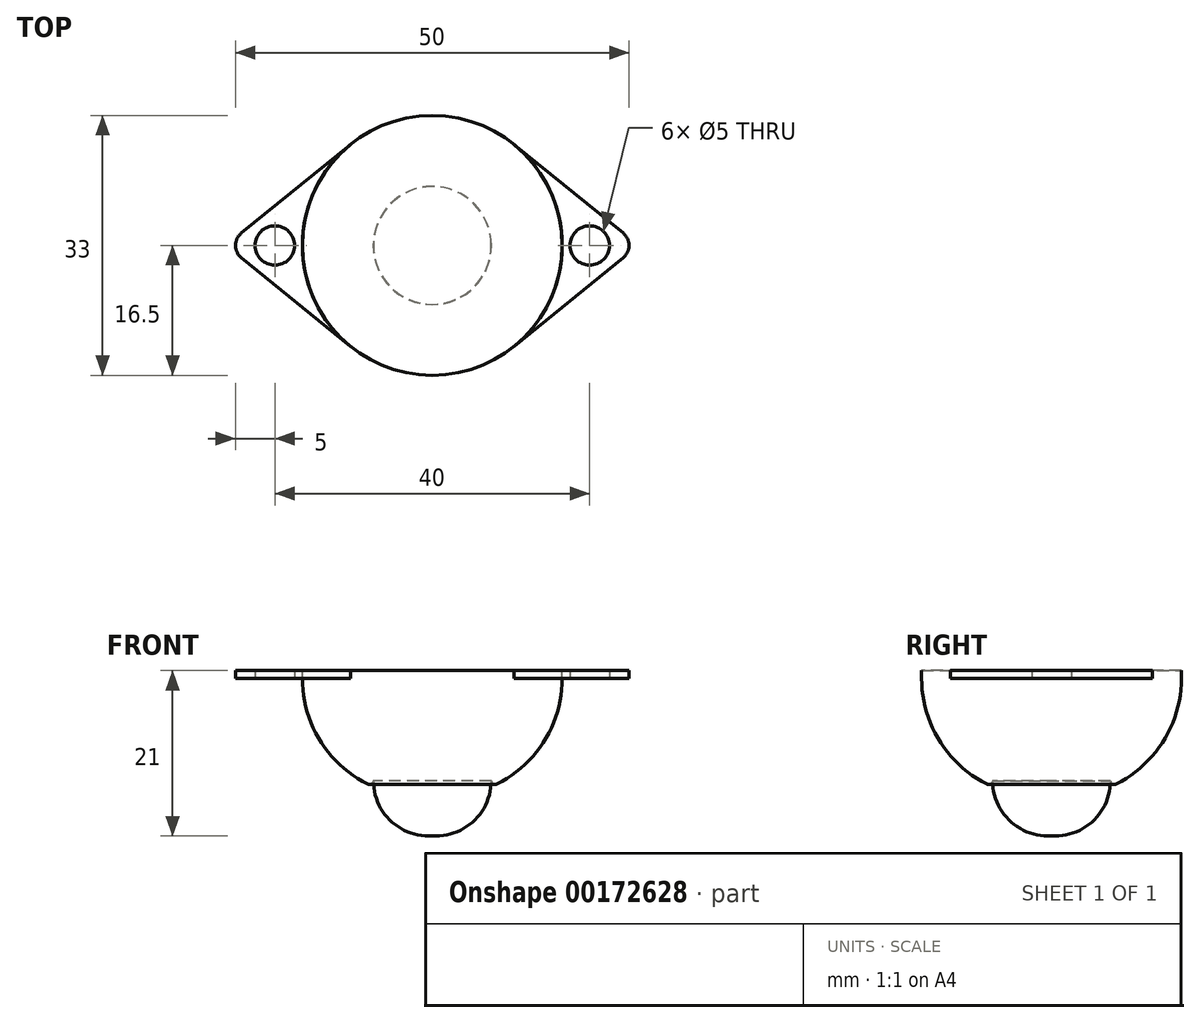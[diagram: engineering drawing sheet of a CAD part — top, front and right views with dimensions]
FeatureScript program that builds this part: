
annotation { "Feature Type Name" : "Feature", "Feature Type Description" : "" }
export const myFeature = defineFeature(function(context is Context, id is Id, definition is map)
    precondition{}
    {
        {
            var Q0;
            Q0=qCreatedBy(makeId("Top.planeOp"),FACE);
            var sketch = newSketch(context, id + "F0", { "sketchPlane" : qUnion([Q0])});
            skCircle(sketch, "E0", {"center": v(0, 0) * mm, "radius": 16.5 * mm});
            skPoint(sketch, "E1", {"position": v(-25, 0) * mm});
            skPoint(sketch, "E2.MirrorP", {"position": v(25, 0) * mm});
            skArc(sketch, "E3", {"start": v(-24.26, 1.55) * mm, "mid": v(-25, 0) * mm, "end": v(-24.26, -1.55) * mm});
            skArc(sketch, "E4", {"start": v(24.26, -1.55) * mm, "mid": v(25, 0) * mm, "end": v(24.26, 1.55) * mm});
            skLineSegment(sketch, "E5", {"start": v(-24.26, 1.55) * mm, "end": v(-10.4, 12.8) * mm});
            skLineSegment(sketch, "E6", {"start": v(-24.26, -1.55) * mm, "end": v(-10.4, -12.8) * mm});
            skLineSegment(sketch, "E7", {"start": v(10.4, 12.8) * mm, "end": v(24.26, 1.55) * mm});
            skPoint(sketch, "E8", {"position": v(-24.26, 1.55) * mm});
            skPoint(sketch, "E9", {"position": v(-24.26, -1.55) * mm});
            skPoint(sketch, "E10", {"position": v(24.26, 1.55) * mm});
            skLineSegment(sketch, "E11", {"start": v(24.26, -1.55) * mm, "end": v(10.4, -12.8) * mm});
            skPoint(sketch, "E12", {"position": v(24.26, -1.55) * mm});
            skSolve(sketch);
        }
        {
            var Q0;
            Q0=makeQuery(id+"F0.imprint","IMPRINT",FACE,{"disambiguationData":[TD([[makeQuery(id+"F0.imprint","IMPRINT",EDGE,{"derivedFrom":sQuery(id+"F0.wireOp",EDGE,"E3")}),1.0]])]});
            var Q1;
            Q1=makeQuery(id+"F0.imprint","IMPRINT",FACE,{"disambiguationData":[TD([[makeQuery(id+"F0.imprint","IMPRINT",EDGE,{"derivedFrom":sQuery(id+"F0.wireOp",EDGE,"E4")}),1.0]])]});
            extrude(context, id + "F1", {"entities" : qUnion([Q0, Q1]), "depth" : 1 * mm});
        }
        {
            var Q0;
            {var subQ0=sQuery(id+"F0.wireOp",EDGE,"E0");var subQ1=makeQuery(id+"F0.imprint","INTERSECT",VERTEX,{"derivedFrom":[subQ0,sQuery(id+"F0.wireOp",EDGE,"E5")]});Q0=makeQuery(id+"F0.imprint","IMPRINT",FACE,{"disambiguationData":[TD([[makeQuery(id+"F0.imprint","IMPRINT",EDGE,{"disambiguationData":[TD([[subQ1,1.0]])],"derivedFrom":subQ0}),1.0]])]});}
            extrude(context, id + "F2", {"entities" : qUnion([Q0]), "depth" : 16 * mm});
        }
        {
            var Q0;
            Q0=makeQuery(id+"F2.opExtrude","CAP_EDGE",EDGE,{"disambiguationData":[OSD([sQuery(id+"F0.wireOp",EDGE,"E0")])],"isStart":false});
            fillet(context, id + "F3", {"entities" : qUnion([Q0]), "radius" : 15 * mm, "tangentPropagation" : true, "allowEdgeOverflow" : false});
        }
        {
            var Q0;
            Q0=makeQuery(id+"F2.opExtrude","CAP_FACE",FACE,{"disambiguationData":[OSD([sQuery(id+"F0.wireOp",EDGE,"E0")])],"isStart":false});
            var sketch = newSketch(context, id + "F4", { "sketchPlane" : qUnion([Q0])});
            skCircle(sketch, "E13", {"center": v(0, 0) * mm, "radius": 7.5 * mm});
            skSolve(sketch);
        }
        {
            var Q0;
            Q0 = qSketchRegion(id + "F4", true);
            extrude(context, id + "F5", {"entities" : qUnion([Q0]), "operationType" : NewBodyOperationType.REMOVE, "oppositeDirection" : true, "depth" : 2 * mm});
        }
        {
            var Q0;
            Q0=makeQuery(id+"F5.boolean.opBoolean","INTERSECT",EDGE,{"derivedFrom":[makeQuery(id+"F3.opFillet","BLEND_FACE",FACE,{"disambiguationData":[OSD([sQuery(id+"F0.wireOp",EDGE,"E0")])]}),makeQuery(id+"F5.opExtrude","SWEPT_FACE",FACE,{"disambiguationData":[OSD([sQuery(id+"F4.wireOp",EDGE,"E13")])]})]});
            fillet(context, id + "F6", {"entities" : qUnion([Q0]), "radius" : 0.5 * mm, "tangentPropagation" : true, "allowEdgeOverflow" : false});
        }
        {
            var Q0;
            Q0=makeQuery(id+"F5.boolean.opBoolean","COPY",FACE,{"derivedFrom":makeQuery(id+"F5.opExtrude","CAP_FACE",FACE,{"disambiguationData":[OSD([sQuery(id+"F4.wireOp",EDGE,"E13")])],"isStart":false})});
            var sketch = newSketch(context, id + "F7", { "sketchPlane" : qUnion([Q0])});
            skCircle(sketch, "E14", {"center": v(0, 0) * mm, "radius": 7.48 * mm});
            skSolve(sketch);
        }
        {
            var Q0;
            Q0 = qSketchRegion(id + "F7", true);
            extrude(context, id + "F8", {"entities" : qUnion([Q0]), "operationType" : NewBodyOperationType.ADD, "depth" : 7 * mm});
        }
        {
            var Q0;
            Q0=makeQuery(id+"F8.opExtrude","CAP_FACE",FACE,{"disambiguationData":[OSD([sQuery(id+"F7.wireOp",EDGE,"E14")])],"isStart":false});
            fillet(context, id + "F9", {"entities" : qUnion([Q0]), "radius" : 7 * mm, "tangentPropagation" : true, "allowEdgeOverflow" : false});
        }
        {
            var Q0;
            Q0=makeQuery(id+"F1.opExtrude","CAP_FACE",FACE,{"disambiguationData":[OSD([sQuery(id+"F0.wireOp",EDGE,"E0"),sQuery(id+"F0.wireOp",EDGE,"E3"),sQuery(id+"F0.wireOp",EDGE,"E5"),sQuery(id+"F0.wireOp",EDGE,"E6")])],"isStart":false});
            var sketch = newSketch(context, id + "F10", { "sketchPlane" : qUnion([Q0])});
            skPoint(sketch, "E15", {"position": v(-20, 0) * mm});
            skCircle(sketch, "E16", {"center": v(-20, 0) * mm, "radius": 2.5 * mm});
            skSolve(sketch);
        }
        {
            var Q0;
            Q0=makeQuery(id+"F10.imprint","IMPRINT",FACE,{"disambiguationData":[TD([[makeQuery(id+"F10.imprint","IMPRINT",EDGE,{"derivedFrom":sQuery(id+"F10.wireOp",EDGE,"E16")}),1.0]])]});
            extrude(context, id + "F11", {"entities" : qUnion([Q0]), "operationType" : NewBodyOperationType.REMOVE, "oppositeDirection" : true, "depth" : 25.4 * mm});
        }
        {
            var Q0;
            Q0=makeQuery(id+"F1.opExtrude","CAP_FACE",FACE,{"disambiguationData":[OSD([sQuery(id+"F0.wireOp",EDGE,"E0"),sQuery(id+"F0.wireOp",EDGE,"E4"),sQuery(id+"F0.wireOp",EDGE,"E7"),sQuery(id+"F0.wireOp",EDGE,"E11")])],"isStart":false});
            var sketch = newSketch(context, id + "F12", { "sketchPlane" : qUnion([Q0])});
            skCircle(sketch, "E17", {"center": v(20, 0) * mm, "radius": 2.5 * mm});
            skSolve(sketch);
        }
        {
            var Q0;
            Q0 = qSketchRegion(id + "F12", true);
            extrude(context, id + "F13", {"entities" : qUnion([Q0]), "operationType" : NewBodyOperationType.REMOVE, "oppositeDirection" : true, "depth" : 25.4 * mm});
        }
        {
            var Q0;
            Q0=makeQuery(id+"F2.opExtrude","CAP_FACE",FACE,{"disambiguationData":[OSD([sQuery(id+"F0.wireOp",EDGE,"E0")])],"isStart":true});
            var sketch = newSketch(context, id + "F14", { "sketchPlane" : qUnion([Q0])});
            skLineSegment(sketch, "E18", {"start": v(-76.17, 0) * mm, "end": v(75.9, 0) * mm});
            skSolve(sketch);
        }
        {
            var Q0;
            Q0=makeQuery(id+"F1.opExtrude","SWEPT_BODY",BODY,{"disambiguationData":[OSD([sQuery(id+"F0.wireOp",EDGE,"E0"),sQuery(id+"F0.wireOp",EDGE,"E4"),sQuery(id+"F0.wireOp",EDGE,"E7"),sQuery(id+"F0.wireOp",EDGE,"E11")])]});
            var Q1;
            Q1=makeQuery(id+"F2.opExtrude","SWEPT_BODY",BODY,{"disambiguationData":[OSD([sQuery(id+"F0.wireOp",EDGE,"E0")])]});
            var Q2;
            Q2=makeQuery(id+"F1.opExtrude","SWEPT_BODY",BODY,{"disambiguationData":[OSD([sQuery(id+"F0.wireOp",EDGE,"E0"),sQuery(id+"F0.wireOp",EDGE,"E3"),sQuery(id+"F0.wireOp",EDGE,"E5"),sQuery(id+"F0.wireOp",EDGE,"E6")])]});
            var Q3;
            Q3=sQuery(id+"F14.wireOp",EDGE,"E18");
            transform(context, id + "F15", {"entities" : qUnion([Q0, Q1, Q2]), "transformType" : TransformType.ROTATION, "transformAxis" : qUnion([Q3]), "angle" : 180 * degree, "makeCopy" : false});
        }
    });
